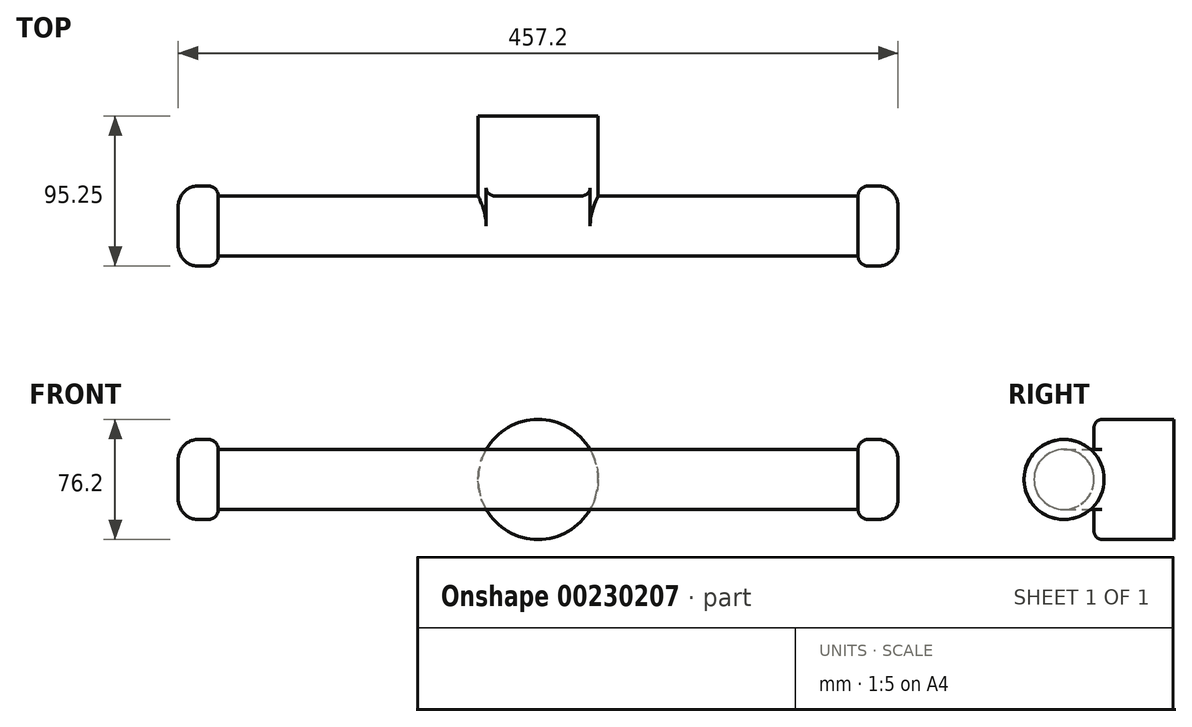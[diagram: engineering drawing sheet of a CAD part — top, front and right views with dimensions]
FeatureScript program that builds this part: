
annotation { "Feature Type Name" : "Feature", "Feature Type Description" : "" }
export const myFeature = defineFeature(function(context is Context, id is Id, definition is map)
    precondition{}
    {
        {
            var Q0;
            Q0=qCreatedBy(makeId("Front.planeOp"),FACE);
            var sketch = newSketch(context, id + "F0", { "sketchPlane" : qUnion([Q0])});
            skCircle(sketch, "E0", {"center": v(0, 0) * mm, "radius": 38.1 * mm});
            skSolve(sketch);
        }
        {
            var Q0;
            Q0 = qSketchRegion(id + "F0", true);
            extrude(context, id + "F1", {"entities" : qUnion([Q0]), "depth" : 50.8 * mm});
        }
        {
            var Q0;
            Q0=makeQuery(id+"F1.opExtrude","CAP_FACE",FACE,{"disambiguationData":[OSD([sQuery(id+"F0.wireOp",EDGE,"E0")])],"isStart":false});
            var sketch = newSketch(context, id + "F2", { "sketchPlane" : qUnion([Q0])});
            skLineSegment(sketch, "E1.bottom", {"start": v(-203.2, 19.05) * mm, "end": v(203.2, 19.05) * mm});
            skLineSegment(sketch, "E1.top", {"start": v(-203.2, -19.05) * mm, "end": v(203.2, -19.05) * mm});
            skLineSegment(sketch, "E1.left", {"start": v(-203.2, 19.05) * mm, "end": v(-203.2, -19.05) * mm});
            skLineSegment(sketch, "E1.right", {"start": v(203.2, 19.05) * mm, "end": v(203.2, -19.05) * mm});
            skPoint(sketch, "E1.middle", {"position": v(0, 0) * mm});
            skSolve(sketch);
        }
        {
            var Q0;
            Q0 = qSketchRegion(id + "F2", true);
            extrude(context, id + "F3", {"entities" : qUnion([Q0]), "operationType" : NewBodyOperationType.ADD, "depth" : 38.1 * mm});
        }
        {
            var Q0;
            Q0=makeQuery(id+"F3.opExtrude","CAP_EDGE",EDGE,{"disambiguationData":[OSD([sQuery(id+"F2.wireOp",EDGE,"E1.bottom")])],"isStart":false});
            var Q1;
            Q1=makeQuery(id+"F3.opExtrude","CAP_EDGE",EDGE,{"disambiguationData":[OSD([sQuery(id+"F2.wireOp",EDGE,"E1.top")])],"isStart":false});
            var Q2;
            {var subQ0=sQuery(id+"F2.wireOp",EDGE,"E1.top");var subQ1=makeQuery(id+"F3.opExtrude","SWEPT_FACE",FACE,{"disambiguationData":[OSD([subQ0])]});var subQ2=sQuery(id+"F2.wireOp",EDGE,"E1.left");var subQ3=makeQuery(id+"F3.opExtrude","CAP_FACE",FACE,{"disambiguationData":[OSD([sQuery(id+"F2.wireOp",EDGE,"E1.bottom"),subQ0,subQ2,sQuery(id+"F2.wireOp",EDGE,"E1.right")])],"isStart":true});Q2=makeQuery(id+"F3.boolean.opBoolean","SPLIT",EDGE,{"disambiguationData":[topologyDisambiguationEdgeConnected([subQ3,subQ1]),TD([makeQuery(id+"F3.opExtrude","SWEPT_FACE",FACE,{"disambiguationData":[OSD([subQ2])]})])],"derivedFrom":makeQuery(id+"F3.opExtrude","CAP_EDGE",EDGE,{"disambiguationData":[OSD([subQ0])],"isStart":true})});}
            var Q3;
            {var subQ0=sQuery(id+"F2.wireOp",EDGE,"E1.left");var subQ1=sQuery(id+"F2.wireOp",EDGE,"E1.bottom");var subQ2=makeQuery(id+"F3.opExtrude","CAP_FACE",FACE,{"disambiguationData":[OSD([subQ1,sQuery(id+"F2.wireOp",EDGE,"E1.top"),subQ0,sQuery(id+"F2.wireOp",EDGE,"E1.right")])],"isStart":true});var subQ4=makeQuery(id+"F3.opExtrude","SWEPT_FACE",FACE,{"disambiguationData":[OSD([subQ1])]});Q3=makeQuery(id+"F3.boolean.opBoolean","SPLIT",EDGE,{"disambiguationData":[topologyDisambiguationEdgeConnected([subQ4,subQ2]),TD([makeQuery(id+"F3.opExtrude","SWEPT_FACE",FACE,{"disambiguationData":[OSD([subQ0])]})])],"derivedFrom":makeQuery(id+"F3.opExtrude","CAP_EDGE",EDGE,{"disambiguationData":[OSD([subQ1])],"isStart":true})});}
            var Q4;
            {var subQ0=sQuery(id+"F2.wireOp",EDGE,"E1.right");var subQ1=sQuery(id+"F2.wireOp",EDGE,"E1.bottom");var subQ2=makeQuery(id+"F3.opExtrude","CAP_FACE",FACE,{"disambiguationData":[OSD([subQ1,sQuery(id+"F2.wireOp",EDGE,"E1.top"),sQuery(id+"F2.wireOp",EDGE,"E1.left"),subQ0])],"isStart":true});var subQ4=makeQuery(id+"F3.opExtrude","SWEPT_FACE",FACE,{"disambiguationData":[OSD([subQ1])]});Q4=makeQuery(id+"F3.boolean.opBoolean","SPLIT",EDGE,{"disambiguationData":[topologyDisambiguationEdgeConnected([subQ4,subQ2]),TD([makeQuery(id+"F3.opExtrude","SWEPT_FACE",FACE,{"disambiguationData":[OSD([subQ0])]})])],"derivedFrom":makeQuery(id+"F3.opExtrude","CAP_EDGE",EDGE,{"disambiguationData":[OSD([subQ1])],"isStart":true})});}
            var Q5;
            {var subQ0=sQuery(id+"F2.wireOp",EDGE,"E1.top");var subQ1=makeQuery(id+"F3.opExtrude","SWEPT_FACE",FACE,{"disambiguationData":[OSD([subQ0])]});var subQ2=sQuery(id+"F2.wireOp",EDGE,"E1.right");var subQ3=makeQuery(id+"F3.opExtrude","CAP_FACE",FACE,{"disambiguationData":[OSD([sQuery(id+"F2.wireOp",EDGE,"E1.bottom"),subQ0,sQuery(id+"F2.wireOp",EDGE,"E1.left"),subQ2])],"isStart":true});Q5=makeQuery(id+"F3.boolean.opBoolean","SPLIT",EDGE,{"disambiguationData":[topologyDisambiguationEdgeConnected([subQ3,subQ1]),TD([makeQuery(id+"F3.opExtrude","SWEPT_FACE",FACE,{"disambiguationData":[OSD([subQ2])]})])],"derivedFrom":makeQuery(id+"F3.opExtrude","CAP_EDGE",EDGE,{"disambiguationData":[OSD([subQ0])],"isStart":true})});}
            fillet(context, id + "F4", {"entities" : qUnion([Q0, Q1, Q2, Q3, Q4, Q5]), "radius" : 19.05 * mm, "tangentPropagation" : true, "allowEdgeOverflow" : false});
        }
        {
            var Q0;
            {var subQ0=sQuery(id+"F0.wireOp",EDGE,"E0");var subQ1=makeQuery(id+"F1.opExtrude","SWEPT_FACE",FACE,{"disambiguationData":[OSD([subQ0])]});var subQ2=makeQuery(id+"F1.opExtrude","CAP_FACE",FACE,{"disambiguationData":[OSD([subQ0])],"isStart":false});var subQ3=sQuery(id+"F2.wireOp",EDGE,"E1.bottom");Q0=makeQuery(id+"F3.boolean.opBoolean","SPLIT",EDGE,{"disambiguationData":[topologyDisambiguationEdgeConnected([subQ1,subQ2]),TD([makeQuery(id+"F3.opExtrude","SWEPT_FACE",FACE,{"disambiguationData":[OSD([subQ3])]})])],"derivedFrom":makeQuery(id+"F1.opExtrude","CAP_EDGE",EDGE,{"disambiguationData":[OSD([subQ0])],"isStart":false})});}
            var Q1;
            {var subQ0=sQuery(id+"F0.wireOp",EDGE,"E0");var subQ1=makeQuery(id+"F1.opExtrude","SWEPT_FACE",FACE,{"disambiguationData":[OSD([subQ0])]});var subQ2=makeQuery(id+"F1.opExtrude","CAP_FACE",FACE,{"disambiguationData":[OSD([subQ0])],"isStart":false});var subQ3=sQuery(id+"F2.wireOp",EDGE,"E1.top");Q1=makeQuery(id+"F3.boolean.opBoolean","SPLIT",EDGE,{"disambiguationData":[topologyDisambiguationEdgeConnected([subQ1,subQ2]),TD([makeQuery(id+"F3.opExtrude","SWEPT_FACE",FACE,{"disambiguationData":[OSD([subQ3])]})])],"derivedFrom":makeQuery(id+"F1.opExtrude","CAP_EDGE",EDGE,{"disambiguationData":[OSD([subQ0])],"isStart":false})});}
            fillet(context, id + "F5", {"entities" : qUnion([Q0, Q1]), "radius" : 5.08 * mm, "tangentPropagation" : true, "allowEdgeOverflow" : false});
        }
        {
            var Q0;
            Q0=makeQuery(id+"F3.opExtrude","SWEPT_FACE",FACE,{"disambiguationData":[OSD([sQuery(id+"F2.wireOp",EDGE,"E1.left")])]});
            var sketch = newSketch(context, id + "F6", { "sketchPlane" : qUnion([Q0])});
            skCircle(sketch, "E2", {"center": v(69.85, 0) * mm, "radius": 25.4 * mm});
            skSolve(sketch);
        }
        {
            var Q0;
            Q0 = qSketchRegion(id + "F6", true);
            extrude(context, id + "F7", {"entities" : qUnion([Q0]), "operationType" : NewBodyOperationType.ADD, "depth" : 25.4 * mm});
        }
        {
            var Q0;
            Q0=makeQuery(id+"F3.opExtrude","SWEPT_FACE",FACE,{"disambiguationData":[OSD([sQuery(id+"F2.wireOp",EDGE,"E1.right")])]});
            var sketch = newSketch(context, id + "F8", { "sketchPlane" : qUnion([Q0])});
            skCircle(sketch, "E3", {"center": v(-69.85, 0) * mm, "radius": 25.4 * mm});
            skSolve(sketch);
        }
        {
            var Q0;
            Q0 = qSketchRegion(id + "F8", true);
            extrude(context, id + "F9", {"entities" : qUnion([Q0]), "operationType" : NewBodyOperationType.ADD, "depth" : 25.4 * mm});
        }
        {
            var Q0;
            Q0=makeQuery(id+"F9.opExtrude","CAP_EDGE",EDGE,{"disambiguationData":[OSD([sQuery(id+"F8.wireOp",EDGE,"E3")])],"isStart":true});
            var Q1;
            Q1=makeQuery(id+"F7.opExtrude","CAP_EDGE",EDGE,{"disambiguationData":[OSD([sQuery(id+"F6.wireOp",EDGE,"E2")])],"isStart":true});
            fillet(context, id + "F10", {"entities" : qUnion([Q0, Q1]), "radius" : 6.35 * mm, "tangentPropagation" : true, "allowEdgeOverflow" : false});
        }
        {
            var Q0;
            Q0=makeQuery(id+"F9.opExtrude","CAP_EDGE",EDGE,{"disambiguationData":[OSD([sQuery(id+"F8.wireOp",EDGE,"E3")])],"isStart":false});
            var Q1;
            Q1=makeQuery(id+"F7.opExtrude","CAP_EDGE",EDGE,{"disambiguationData":[OSD([sQuery(id+"F6.wireOp",EDGE,"E2")])],"isStart":false});
            fillet(context, id + "F11", {"entities" : qUnion([Q0, Q1]), "radius" : 12.7 * mm, "tangentPropagation" : true, "allowEdgeOverflow" : false});
        }
    });
